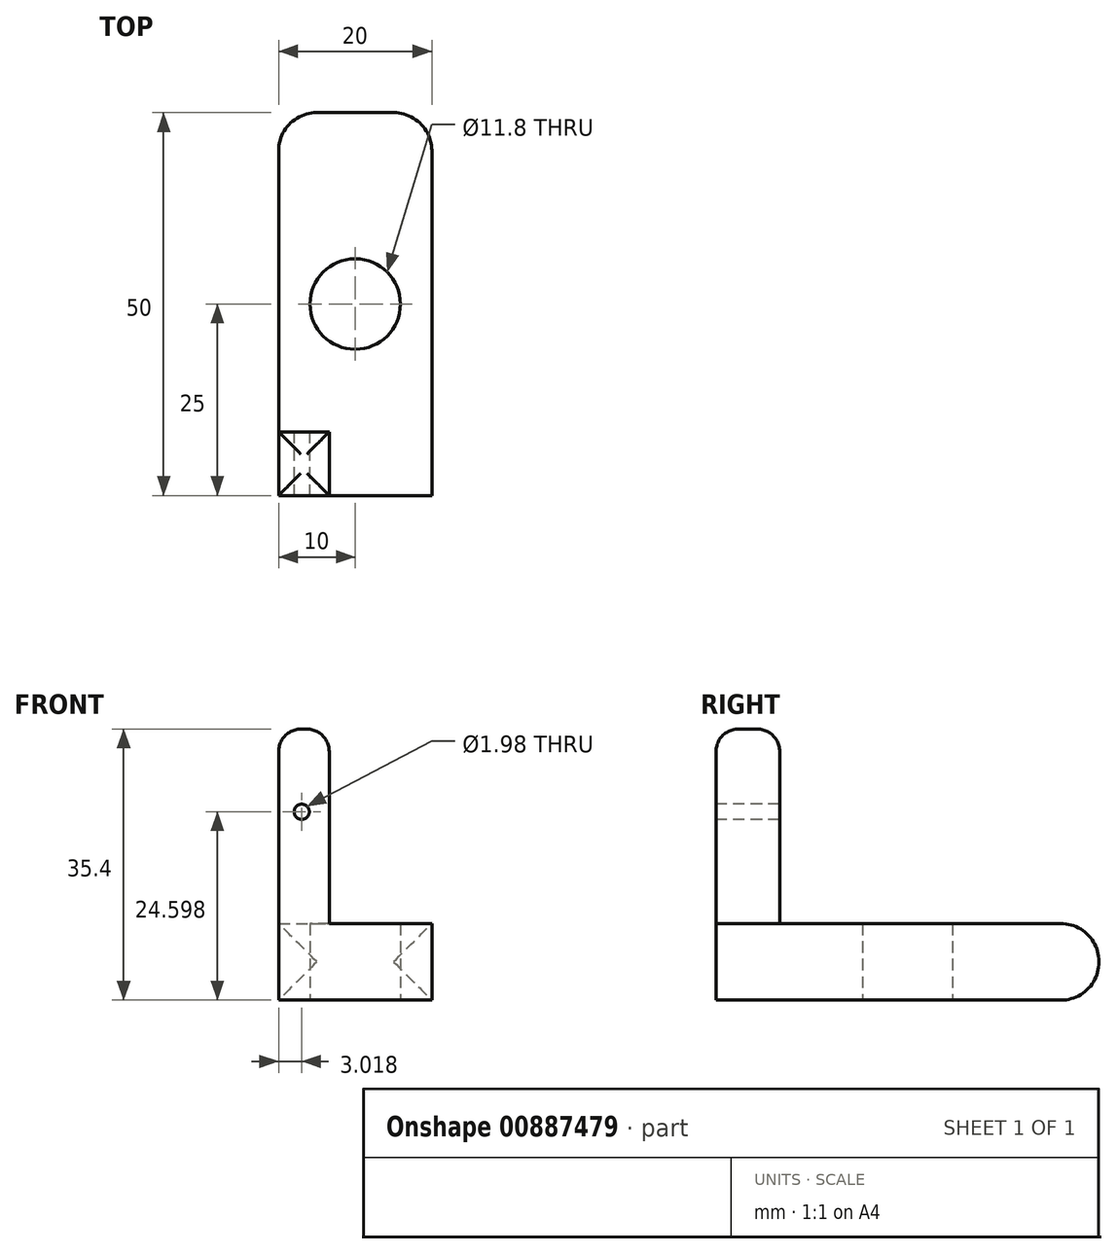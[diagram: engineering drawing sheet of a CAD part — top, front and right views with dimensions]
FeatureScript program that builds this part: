
annotation { "Feature Type Name" : "Feature", "Feature Type Description" : "" }
export const myFeature = defineFeature(function(context is Context, id is Id, definition is map)
    precondition{}
    {
        {
            var Q0;
            Q0=qCreatedBy(makeId("Top.planeOp"),FACE);
            var sketch = newSketch(context, id + "F0", { "sketchPlane" : qUnion([Q0])});
            skLineSegment(sketch, "E0.bottom", {"start": v(10, -25) * mm, "end": v(-10, -25) * mm});
            skLineSegment(sketch, "E0.top", {"start": v(10, 25) * mm, "end": v(-10, 25) * mm});
            skLineSegment(sketch, "E0.left", {"start": v(10, -25) * mm, "end": v(10, 25) * mm});
            skLineSegment(sketch, "E0.right", {"start": v(-10, -25) * mm, "end": v(-10, 25) * mm});
            skPoint(sketch, "E0.middle", {"position": v(0, 0) * mm});
            skCircle(sketch, "E1", {"center": v(0, 0) * mm, "radius": 5.9 * mm});
            skSolve(sketch);
        }
        {
            var Q0;
            Q0=makeQuery(id+"F0.imprint","IMPRINT",FACE,{"disambiguationData":[TD([[makeQuery(id+"F0.imprint","IMPRINT",EDGE,{"derivedFrom":sQuery(id+"F0.wireOp",EDGE,"E0.bottom")}),-1.0]])]});
            extrude(context, id + "F1", {"entities" : qUnion([Q0]), "depth" : 10 * mm, "offsetDistance" : 25.4 * mm});
        }
        {
            var Q0;
            Q0=makeQuery(id+"F1.opExtrude","CAP_FACE",FACE,{"disambiguationData":[OSD([sQuery(id+"F0.wireOp",EDGE,"E0.bottom"),sQuery(id+"F0.wireOp",EDGE,"E0.top"),sQuery(id+"F0.wireOp",EDGE,"E0.left"),sQuery(id+"F0.wireOp",EDGE,"E0.right"),sQuery(id+"F0.wireOp",EDGE,"E1")])],"isStart":false});
            var sketch = newSketch(context, id + "F2", { "sketchPlane" : qUnion([Q0])});
            skLineSegment(sketch, "E2.bottom", {"start": v(-10, -25) * mm, "end": v(-3.4, -25) * mm});
            skLineSegment(sketch, "E2.top", {"start": v(-10, -16.68) * mm, "end": v(-3.4, -16.68) * mm});
            skLineSegment(sketch, "E2.left", {"start": v(-10, -25) * mm, "end": v(-10, -16.68) * mm});
            skLineSegment(sketch, "E2.right", {"start": v(-3.4, -25) * mm, "end": v(-3.4, -16.68) * mm});
            skSolve(sketch);
        }
        {
            var Q0;
            Q0=makeQuery(id+"F2.imprint","IMPRINT",FACE,{"disambiguationData":[TD([[makeQuery(id+"F2.imprint","IMPRINT",EDGE,{"derivedFrom":sQuery(id+"F2.wireOp",EDGE,"E2.bottom")}),-1.0]])]});
            extrude(context, id + "F3", {"entities" : qUnion([Q0]), "operationType" : NewBodyOperationType.ADD, "depth" : 25.4 * mm, "offsetDistance" : 25.4 * mm});
        }
        {
            var Q0;
            Q0=makeQuery(id+"F3.opExtrude","CAP_FACE",FACE,{"disambiguationData":[OSD([sQuery(id+"F2.wireOp",EDGE,"E2.bottom"),sQuery(id+"F2.wireOp",EDGE,"E2.top"),sQuery(id+"F2.wireOp",EDGE,"E2.left"),sQuery(id+"F2.wireOp",EDGE,"E2.right")])],"isStart":false});
            fillet(context, id + "F4", {"entities" : qUnion([Q0]), "radius" : 2.92 * mm, "tangentPropagation" : true, "allowEdgeOverflow" : false});
        }
        {
            var Q0;
            Q0=makeQuery(id+"F1.opExtrude","SWEPT_FACE",FACE,{"disambiguationData":[OSD([sQuery(id+"F0.wireOp",EDGE,"E0.top")])]});
            fillet(context, id + "F5", {"entities" : qUnion([Q0]), "radius" : 4.97 * mm, "tangentPropagation" : true, "allowEdgeOverflow" : false});
        }
        {
            var Q0;
            Q0=makeQuery(id+"F3.boolean.opBoolean","MERGE",FACE,{"derivedFrom":[makeQuery(id+"F1.opExtrude","SWEPT_FACE",FACE,{"disambiguationData":[OSD([sQuery(id+"F0.wireOp",EDGE,"E0.bottom")])]}),makeQuery(id+"F3.opExtrude","SWEPT_FACE",FACE,{"disambiguationData":[OSD([sQuery(id+"F2.wireOp",EDGE,"E2.bottom")])]})]});
            var sketch = newSketch(context, id + "F6", { "sketchPlane" : qUnion([Q0])});
            skCircle(sketch, "E3", {"center": v(-6.98, 24.6) * mm, "radius": 1 * mm});
            skSolve(sketch);
        }
        {
            var Q0;
            Q0=makeQuery(id+"F6.imprint","IMPRINT",FACE,{"disambiguationData":[TD([[makeQuery(id+"F6.imprint","IMPRINT",EDGE,{"derivedFrom":sQuery(id+"F6.wireOp",EDGE,"E3")}),1.0]])]});
            extrude(context, id + "F7", {"entities" : qUnion([Q0]), "operationType" : NewBodyOperationType.REMOVE, "oppositeDirection" : true, "depth" : 9.02 * mm, "offsetDistance" : 25.4 * mm});
        }
    });
